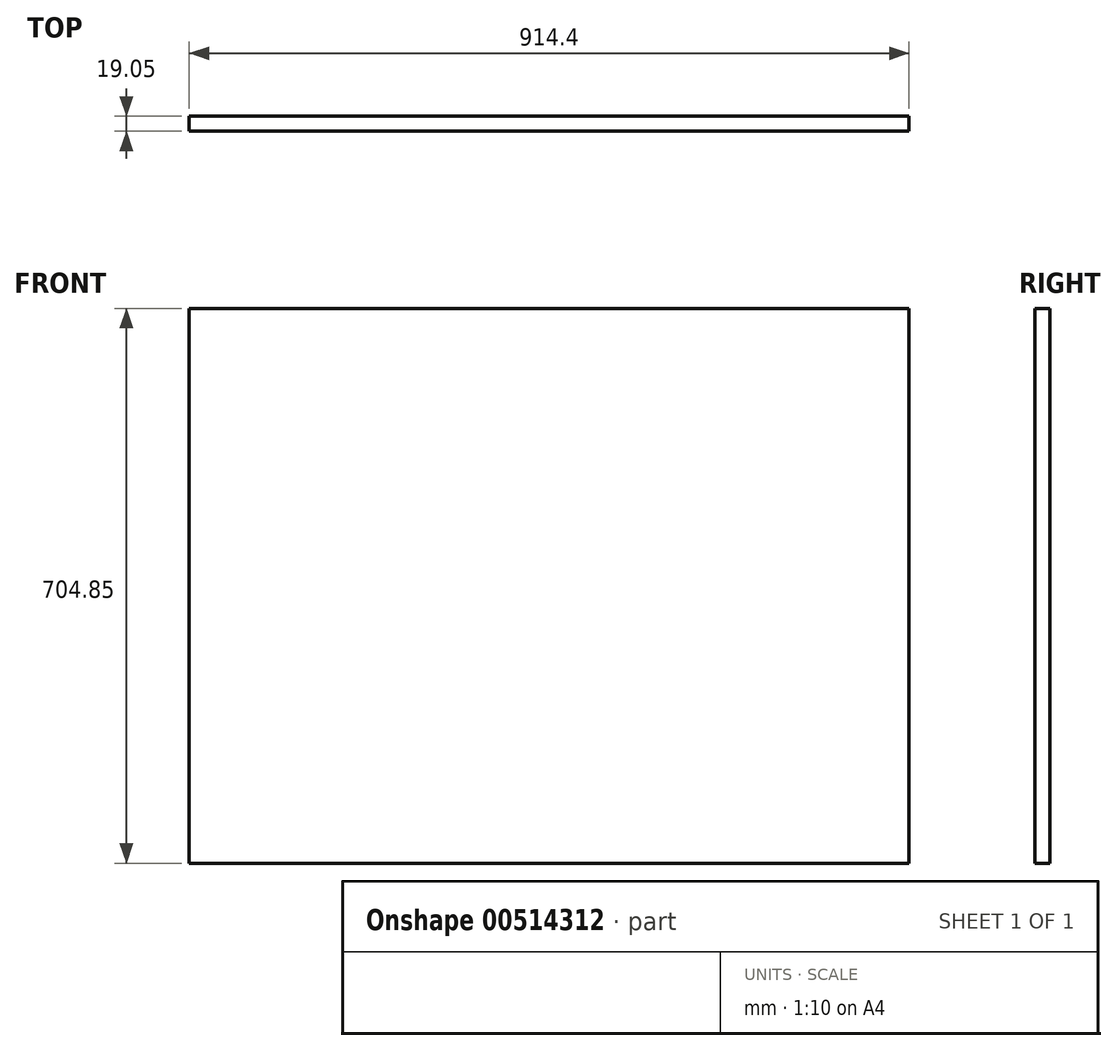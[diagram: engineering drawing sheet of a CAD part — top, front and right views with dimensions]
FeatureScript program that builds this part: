
annotation { "Feature Type Name" : "Feature", "Feature Type Description" : "" }
export const myFeature = defineFeature(function(context is Context, id is Id, definition is map)
    precondition{}
    {
        {
            var Q0;
            Q0=qCreatedBy(makeId("Top.planeOp"),FACE);
            var sketch = newSketch(context, id + "F0", { "sketchPlane" : qUnion([Q0])});
            skLineSegment(sketch, "E0.bottom", {"start": v(710.31, 0) * mm, "end": v(-204.09, 0) * mm});
            skLineSegment(sketch, "E0.top", {"start": v(710.31, 19.05) * mm, "end": v(-204.09, 19.05) * mm});
            skLineSegment(sketch, "E0.left", {"start": v(710.31, 0) * mm, "end": v(710.31, 19.05) * mm});
            skLineSegment(sketch, "E0.right", {"start": v(-204.09, 0) * mm, "end": v(-204.09, 19.05) * mm});
            skPoint(sketch, "E0.middle", {"position": v(253.11, 9.52) * mm});
            skSolve(sketch);
        }
        {
            var Q0;
            Q0 = qSketchRegion(id + "F0", true);
            extrude(context, id + "F1", {"entities" : qUnion([Q0]), "depth" : 704.85 * mm});
        }
    });
